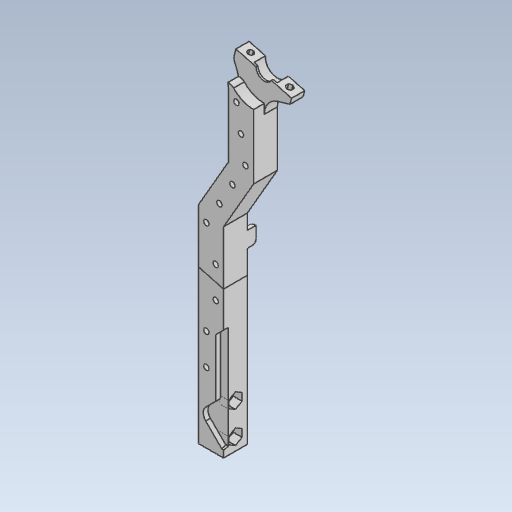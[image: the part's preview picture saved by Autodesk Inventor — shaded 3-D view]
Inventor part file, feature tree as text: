
AUTODESK INVENTOR PART (.ipt)
format: ipt  version: 2021.2 (Build 252289000, 289)  size: 380,416 bytes
history: native  units: mm
features: other x10, chamfer x2, fillet x1
ambient origin geometry x8: Origin, YZ Plane, XZ Plane, XY Plane, X Axis, Y Axis, Z Axis, Center Point
bodies: Body1 (feature_tree), Body2 (feature_tree)
feature tree (13):
  other  "Твёрдое тело.ipt"
  other  "РабПлоскость1"
  other  "Разделение1"
  fillet  "Сопряжение1"  Radius=10.0mm
  chamfer  "Фаска1"  Distance=1.0mm
  chamfer  "Фаска2"  Distance=2.0mm
  other  "Ножка 2::Твёрдое тело.ipt"
  other  "Элемент создания тегов1"
  other  "Твердое тело24::Твёрдое тело.ipt"
  other  "Твердое тело25::Твёрдое тело.ipt"
  other  "Твердое тело1"
  other  "Твердое тело2"
  other  "Твердое тело3"
